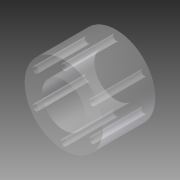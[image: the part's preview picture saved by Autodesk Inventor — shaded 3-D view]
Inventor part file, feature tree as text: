
AUTODESK INVENTOR PART (.ipt)
format: ipt  version: 2014 SP1 (Build 180222100, 222)  size: 106,496 bytes
history: native  units: in
note: dims shown in document units (in); Inventor stores cm internally (conversion verified against a paired STEP export)
features: extrude x1, sketch x1
ambient origin geometry x8: Origin, YZ Plane, XZ Plane, XY Plane, X Axis, Y Axis, Z Axis, Center Point
bodies: Solid1 (feature_tree)
feature tree (2):
  extrude  "Extrusion1"  Depth=1.5in
  sketch  "Sketch1"  dims[d0=1.25in d1=1.875in d2=0.177in d3=2.3622in d5=360.0deg d7=2.25in d8=1.5in d9=0.0in]
